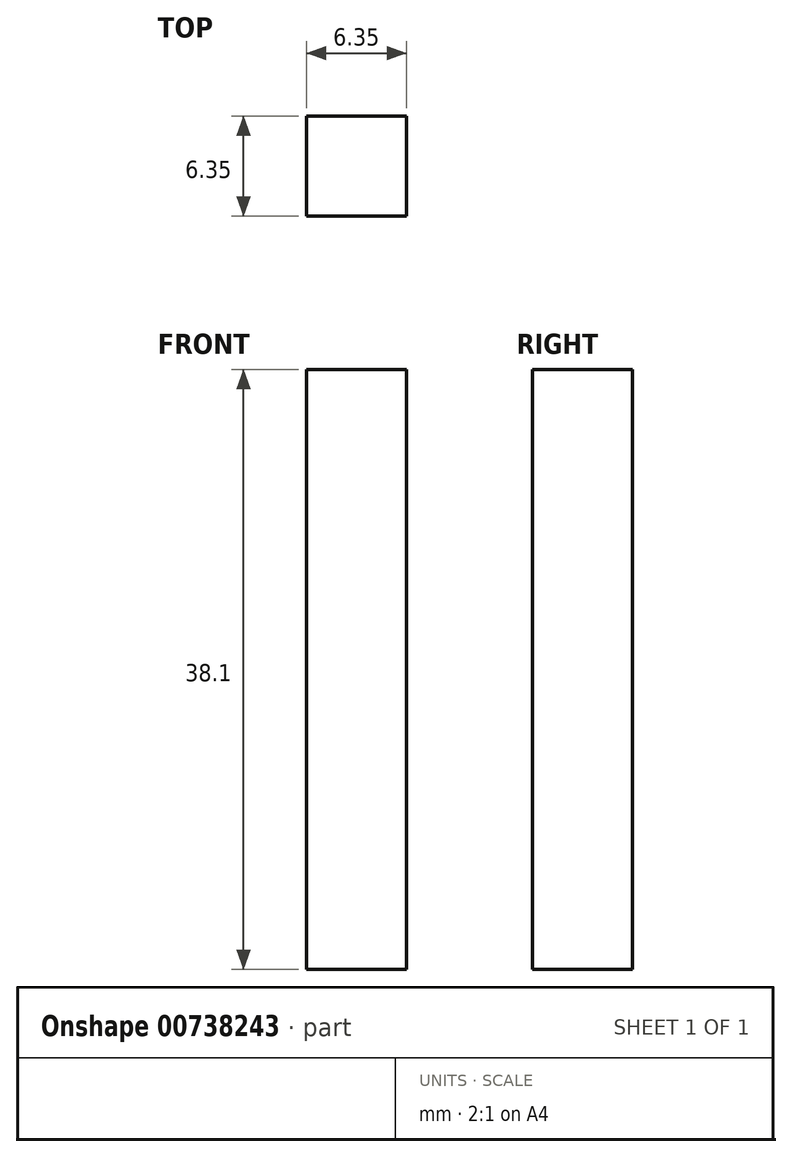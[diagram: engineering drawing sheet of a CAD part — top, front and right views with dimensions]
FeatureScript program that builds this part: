
annotation { "Feature Type Name" : "Feature", "Feature Type Description" : "" }
export const myFeature = defineFeature(function(context is Context, id is Id, definition is map)
    precondition{}
    {
        {
            var Q0;
            Q0=qCreatedBy(makeId("Right.planeOp"),FACE);
            var sketch = newSketch(context, id + "F0", { "sketchPlane" : qUnion([Q0])});
            skLineSegment(sketch, "E0", {"start": v(12.95, 36.83) * mm, "end": v(12.95, -1.27) * mm});
            skLineSegment(sketch, "E1", {"start": v(12.95, -1.27) * mm, "end": v(19.3, -1.27) * mm});
            skLineSegment(sketch, "E2", {"start": v(19.3, -1.27) * mm, "end": v(19.3, 36.83) * mm});
            skLineSegment(sketch, "E3", {"start": v(19.3, 36.83) * mm, "end": v(12.95, 36.83) * mm});
            skSolve(sketch);
        }
        {
            var Q0;
            Q0=makeQuery(id+"F0.imprint","IMPRINT",FACE,{"disambiguationData":[TD([[makeQuery(id+"F0.imprint","IMPRINT",EDGE,{"derivedFrom":sQuery(id+"F0.wireOp",EDGE,"E0")}),1.0]])]});
            extrude(context, id + "F1", {"entities" : qUnion([Q0]), "depth" : 6.35 * mm, "offsetDistance" : 25.4 * mm});
        }
    });
